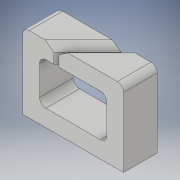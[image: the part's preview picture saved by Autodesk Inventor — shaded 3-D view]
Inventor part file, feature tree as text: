
AUTODESK INVENTOR PART (.ipt)
format: ipt  version: 2019 (Build 230136000, 136)  size: 141,312 bytes
history: native  units: mm
features: extrude x2, sketch x2, chamfer x1, fillet x1
ambient origin geometry x8: Origin, YZ Plane, XZ Plane, XY Plane, X Axis, Y Axis, Z Axis, Center Point
bodies: Solid1 (feature_tree)
feature tree (6):
  extrude  "Extrusion1"  Depth=2.0mm
  extrude  "Extrusion2"  Depth=0.75mm
  chamfer  "Chamfer1"  Distance=2.0mm
  fillet  "Fillet1"  Radius=1.25mm
  sketch  "Sketch1"  dims[d0=2.0mm d1=2.5mm]
  sketch  "Sketch2"  dims[d2=2.5mm d3=1.25mm d4=2.0mm d5=1.25mm d6=1.0mm d7=5.0mm d8=8.0mm d9=2.0mm d10=4.0mm d11=0.0mm d12=2.0mm d13=2.0mm d15=0.3mm d16=0.3mm d17=4.0mm d18=0.0mm d19=0.75mm d20=2.0mm d21=45.0deg d22=0.75mm d23=0.75mm]
